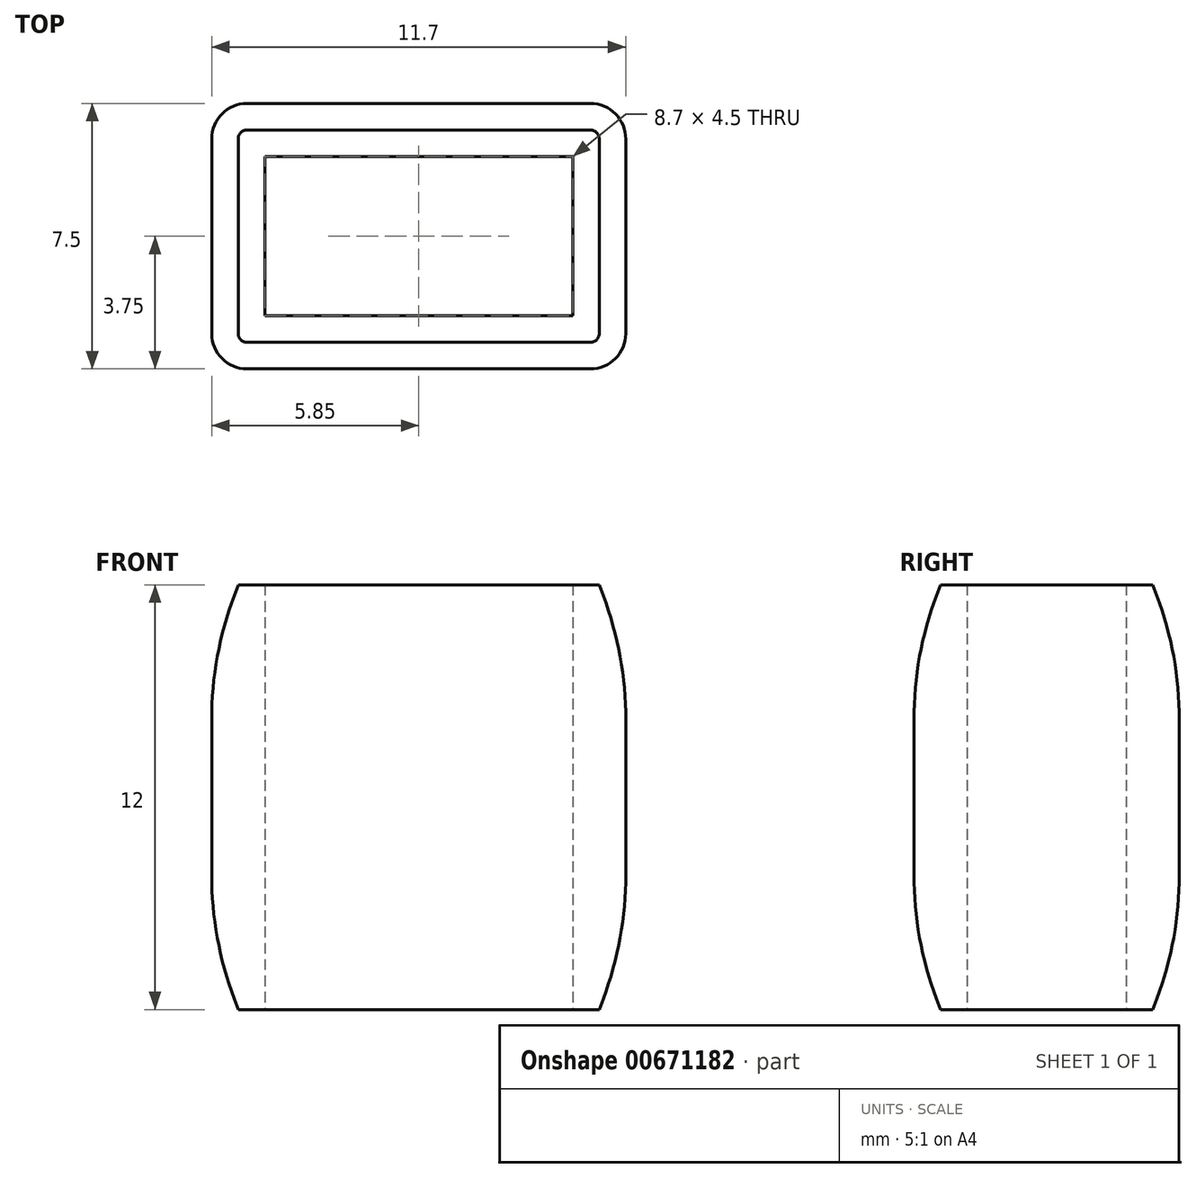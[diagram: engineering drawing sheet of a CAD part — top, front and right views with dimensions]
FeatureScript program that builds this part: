
annotation { "Feature Type Name" : "Feature", "Feature Type Description" : "" }
export const myFeature = defineFeature(function(context is Context, id is Id, definition is map)
    precondition{}
    {
        {
            var Q0;
            Q0=qCreatedBy(makeId("Top.planeOp"),FACE);
            var sketch = newSketch(context, id + "F0", { "sketchPlane" : qUnion([Q0])});
            skLineSegment(sketch, "E0.bottom", {"start": v(4.35, -2.25) * mm, "end": v(-4.35, -2.25) * mm});
            skLineSegment(sketch, "E0.top", {"start": v(4.35, 2.25) * mm, "end": v(-4.35, 2.25) * mm});
            skLineSegment(sketch, "E0.left", {"start": v(4.35, -2.25) * mm, "end": v(4.35, 2.25) * mm});
            skLineSegment(sketch, "E0.right", {"start": v(-4.35, -2.25) * mm, "end": v(-4.35, 2.25) * mm});
            skPoint(sketch, "E0.middle", {"position": v(0, 0) * mm});
            skLineSegment(sketch, "E1.bottom", {"start": v(5.85, -3.75) * mm, "end": v(-5.85, -3.75) * mm});
            skLineSegment(sketch, "E1.top", {"start": v(5.85, 3.75) * mm, "end": v(-5.85, 3.75) * mm});
            skLineSegment(sketch, "E1.left", {"start": v(5.85, -3.75) * mm, "end": v(5.85, 3.75) * mm});
            skLineSegment(sketch, "E1.right", {"start": v(-5.85, -3.75) * mm, "end": v(-5.85, 3.75) * mm});
            skSolve(sketch);
        }
        {
            var Q0;
            Q0 = qSketchRegion(id + "F0", true);
            extrude(context, id + "F1", {"entities" : qUnion([Q0]), "depth" : 12 * mm, "offsetDistance" : 25 * mm});
        }
        {
            var Q0;
            Q0=makeQuery(id+"F1.opExtrude","SWEPT_EDGE",EDGE,{"disambiguationData":[OSD([sQuery(id+"F0.wireOp",EDGE,"E1.bottom"),sQuery(id+"F0.wireOp",EDGE,"E1.left")])]});
            var Q1;
            Q1=makeQuery(id+"F1.opExtrude","SWEPT_EDGE",EDGE,{"disambiguationData":[OSD([sQuery(id+"F0.wireOp",EDGE,"E1.bottom"),sQuery(id+"F0.wireOp",EDGE,"E1.right")])]});
            var Q2;
            Q2=makeQuery(id+"F1.opExtrude","SWEPT_EDGE",EDGE,{"disambiguationData":[OSD([sQuery(id+"F0.wireOp",EDGE,"E1.top"),sQuery(id+"F0.wireOp",EDGE,"E1.right")])]});
            var Q3;
            Q3=makeQuery(id+"F1.opExtrude","SWEPT_EDGE",EDGE,{"disambiguationData":[OSD([sQuery(id+"F0.wireOp",EDGE,"E1.top"),sQuery(id+"F0.wireOp",EDGE,"E1.left")])]});
            fillet(context, id + "F2", {"entities" : qUnion([Q0, Q1, Q2, Q3]), "radius" : 1 * mm, "tangentPropagation" : true, "allowEdgeOverflow" : false});
        }
        {
            var Q0;
            Q0=makeQuery(id+"F1.opExtrude","CAP_EDGE",EDGE,{"disambiguationData":[OSD([sQuery(id+"F0.wireOp",EDGE,"E1.bottom")])],"isStart":false});
            var Q1;
            Q1=makeQuery(id+"F1.opExtrude","CAP_EDGE",EDGE,{"disambiguationData":[OSD([sQuery(id+"F0.wireOp",EDGE,"E1.bottom")])],"isStart":true});
            chamfer(context, id + "F3", {"entities" : qUnion([Q0, Q1]), "chamferType" : ChamferType.TWO_OFFSETS, "width1" : .75 * mm, "oppositeDirection" : true, "width2" : 2 * mm, "tangentPropagation" : true});
        }
        {
            var Q0;
            {var subQ0=sQuery(id+"F0.wireOp",EDGE,"E1.bottom");Q0=makeQuery(id+"F3.opChamfer","BLEND_EDGE",EDGE,{"blendedFrom":[makeQuery(id+"F1.opExtrude","CAP_EDGE",EDGE,{"disambiguationData":[OSD([subQ0])],"isStart":true}),makeQuery(id+"F1.opExtrude","SWEPT_FACE",FACE,{"disambiguationData":[OSD([subQ0])]})],"blendedInto":[makeQuery(id+"F1.opExtrude","SWEPT_FACE",FACE,{"disambiguationData":[OSD([subQ0])]})]});}
            var Q1;
            {var subQ0=sQuery(id+"F0.wireOp",EDGE,"E1.bottom");Q1=makeQuery(id+"F3.opChamfer","BLEND_EDGE",EDGE,{"blendedFrom":[makeQuery(id+"F1.opExtrude","CAP_EDGE",EDGE,{"disambiguationData":[OSD([subQ0])],"isStart":false}),makeQuery(id+"F1.opExtrude","SWEPT_FACE",FACE,{"disambiguationData":[OSD([subQ0])]})],"blendedInto":[makeQuery(id+"F1.opExtrude","SWEPT_FACE",FACE,{"disambiguationData":[OSD([subQ0])]})]});}
            fillet(context, id + "F4", {"entities" : qUnion([Q0, Q1]), "radius" : 10 * mm, "tangentPropagation" : true, "allowEdgeOverflow" : false});
        }
    });
